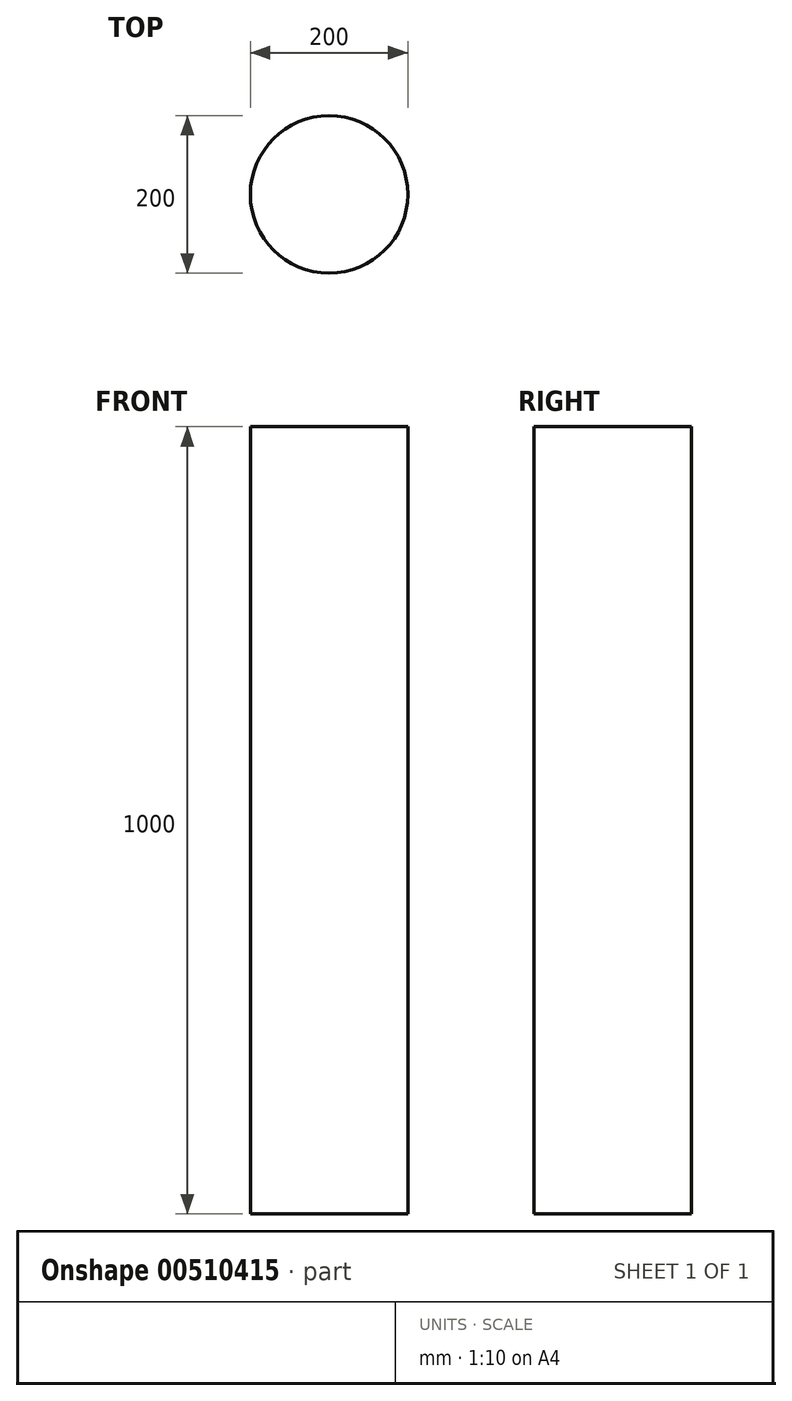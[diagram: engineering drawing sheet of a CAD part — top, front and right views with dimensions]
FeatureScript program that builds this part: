
annotation { "Feature Type Name" : "Feature", "Feature Type Description" : "" }
export const myFeature = defineFeature(function(context is Context, id is Id, definition is map)
    precondition{}
    {
        {
            var Q0;
            Q0=qCreatedBy(makeId("Top.planeOp"),FACE);
            var sketch = newSketch(context, id + "F0", { "sketchPlane" : qUnion([Q0])});
            skCircle(sketch, "E0", {"center": v(0, 0) * mm, "radius": 100 * mm});
            skSolve(sketch);
        }
        {
            var Q0;
            Q0 = qSketchRegion(id + "F0", true);
            extrude(context, id + "F1", {"entities" : qUnion([Q0]), "depth" : 1000 * mm});
        }
    });
